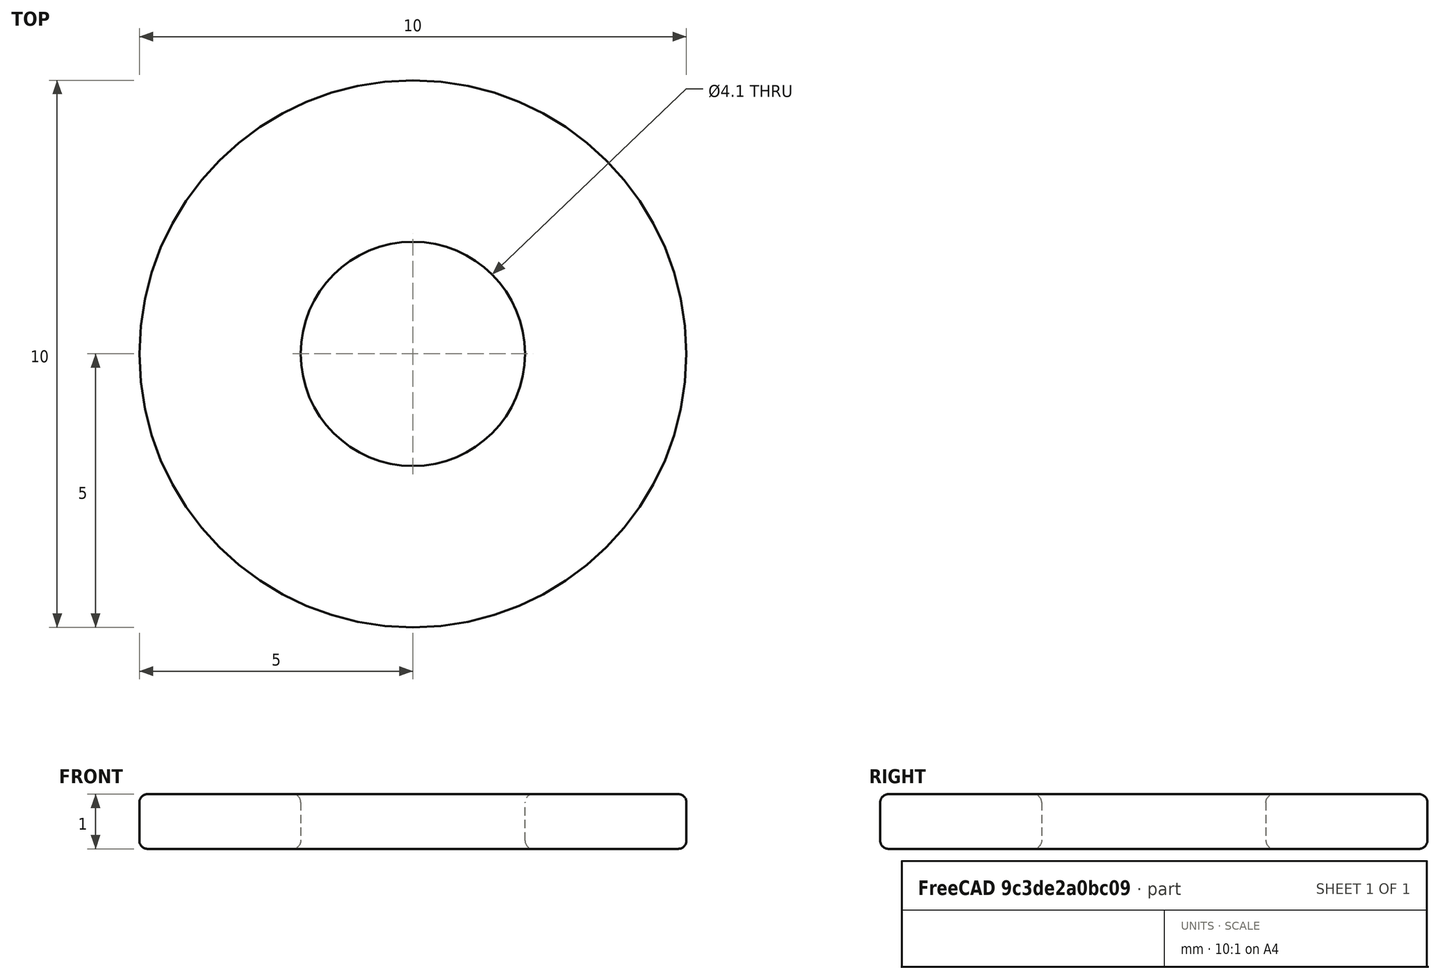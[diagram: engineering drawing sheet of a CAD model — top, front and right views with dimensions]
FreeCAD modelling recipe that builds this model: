
FCSTD DOCUMENT  (FreeCAD 1.0R39319 (Git))
Label: Ring-M4
License: All rights reserved
LicenseURL: http://en.wikipedia.org/wiki/All_rights_reserved
objects: Sketcher::SketchObject×1, PartDesign::Pad×1, PartDesign::Fillet×1, PartDesign::Body×1
note: 9 computed .brp shape members not serialized (recipe doc carries the construction recipe); baked Part::Feature solids carry a one-line shape summary decoded from their .brp

FEATURE [Sketcher::SketchObject] Sketch
  ArcFitTolerance = 0
  AttachmentSupport = -> [XY_Plane]
  FullyConstrained = true
  MakeInternals = false
  MapMode = 5
  sketch-geometry (2):
    g0: Circle CenterX=0 CenterY=0 CenterZ=0 NormalX=0 NormalY=0 NormalZ=1 AngleXU=0 Radius=5
    g1: Circle CenterX=0 CenterY=0 CenterZ=0 NormalX=0 NormalY=0 NormalZ=1 AngleXU=0 Radius=2.05
  constraints (4):
    c: Coincident(g0,g-1)
    c: Coincident(g1,g0)
    c: Diameter(g0) = 10
    c: Diameter(g1) = 4.1
FEATURE [PartDesign::Pad] Pad
  AllowMultiFace = false
  Direction = (0,0,1)
  Length = 1
  Length2 = 100
  Profile = -> Sketch
  Suppressed = false
  Type = 0
FEATURE [PartDesign::Fillet] Fillet
  Base = -> Pad [Edge3,Edge2,Edge6,Edge5]
  BaseFeature = -> Pad
  Radius = 0.15
  Refine = true
  SupportTransform = false
  Suppressed = false
  UseAllEdges = false
FEATURE [PartDesign::Body] Body
  AllowCompound = false
  Group = -> [Sketch,Pad,Fillet]
  Origin = -> Origin
  Tip = -> Fillet
